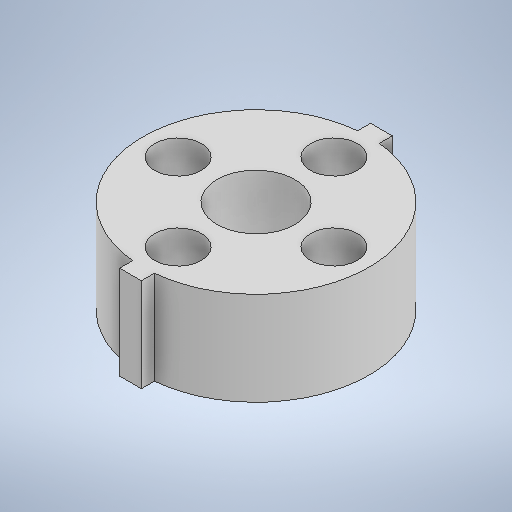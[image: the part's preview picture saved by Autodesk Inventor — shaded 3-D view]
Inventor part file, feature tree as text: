
AUTODESK INVENTOR PART (.ipt)
format: ipt  version: 2025.2 (Build 292293000, 293)  size: 244,224 bytes
history: native  units: in
note: dims shown in document units (in); Inventor stores cm internally (conversion verified against a paired STEP export)
features: sketch x3, extrude x2
ambient origin geometry x8: Origin, YZ Plane, XZ Plane, XY Plane, X Axis, Y Axis, Z Axis, Center Point
bodies: Solid1 (feature_tree)
feature tree (5):
  extrude  "Extrusion1"  Depth=0.0276in
  extrude  "Extrusion2"  Depth=0.2362in
  sketch  "Sketch1"  dims[d0=0.0315in d1=0.0276in]
  sketch  "Sketch2"  dims[d5=0.3937in d6=0.1181in d7=1.5748in d9=360.0deg d11=0.2362in d12=0.0in d13=0.5709in]
  sketch  "Sketch Circular Pattern1"  dims[d2=0.2362in d3=0.0in d4=0.1969in]
